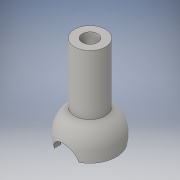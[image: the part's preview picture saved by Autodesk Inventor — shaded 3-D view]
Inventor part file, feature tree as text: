
AUTODESK INVENTOR PART (.ipt)
format: ipt  version: 2016 (Build 200138000, 138)  size: 162,816 bytes
history: native  units: in
note: dims shown in document units (in); Inventor stores cm internally (conversion verified against a paired STEP export)
features: sketch x10, plane x6, extrude x3, revolve x3, loft x2
ambient origin geometry x8: Origin, YZ Plane, XZ Plane, XY Plane, X Axis, Y Axis, Z Axis, Center Point
bodies: Body1 (feature_tree)
feature tree (24):
  sketch  "Sketch1"  dims[d0=0.5in d6=3.0in d7=0.0in]
  extrude  "Extrusion2"  Depth=3.0in TaperAngle=0.0deg
  plane  "Work Plane1"
  sketch  "Sketch9"  dims[d11=-0.125in d22=0.25in]
  plane  "Work Plane2"
  loft  "Loft1"
  sketch  "Sketch11"  dims[d25=0.0in d26=90.0deg d27=0.0in d28=90.0deg]
  revolve  "Revolution8"  [1 undecoded]
  revolve  "Revolution9"  Angle=90.0deg
  plane  "Work Plane4"
  revolve  "Revolution10"  Angle=90.0deg
  extrude  "Extrusion7"  [1 undecoded]
  plane  "Work Plane8"
  extrude  "Extrusion8"  Depth=1.0in TaperAngle=0.0deg
  sketch  "Sketch19"  dims[d51=0.25in]
  plane  "Work Plane9"
  loft  "Loft2"
  sketch  "Sketch10"  dims[d23=-0.185in d24=0.23in]
  sketch  "Sketch15"  dims[d29=0.72in d39=90.0deg]
  sketch  "Sketch16"  dims[d40=90.0deg d41=-2.9375in]
  sketch  "Sketch17"  dims[d42=180.0deg d43=1.0in d44=0.0in]
  plane  "Work Plane7"
  sketch  "Sketch18"  dims[d47=-0.1225in d48=1.462in d49=2.0in d50=0.0in]
  sketch  "Sketch20"  dims[d52=-0.185in d53=0.23in d54=0.0in d55=90.0deg d56=0.0in d57=90.0deg]
note: 2 required parameter values undecoded (feature->parameter linkage not recoverable at this tier; creation-order binding heuristic only, values carry confidence <= 0.55)